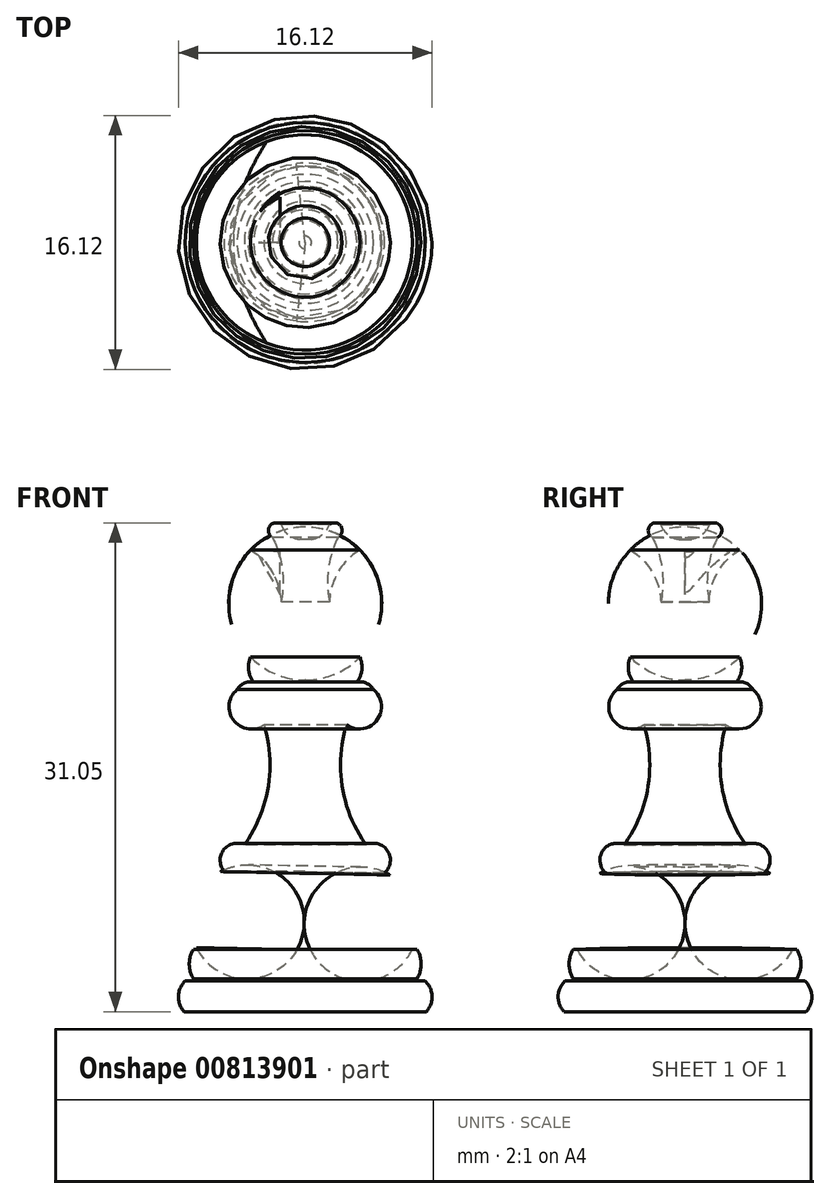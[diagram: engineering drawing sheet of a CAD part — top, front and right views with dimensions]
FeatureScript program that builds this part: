
annotation { "Feature Type Name" : "Feature", "Feature Type Description" : "" }
export const myFeature = defineFeature(function(context is Context, id is Id, definition is map)
    precondition{}
    {
        {
            var Q0;
            Q0=qCreatedBy(makeId("Front.planeOp"),FACE);
            var sketch = newSketch(context, id + "F0", { "sketchPlane" : qUnion([Q0])});
            skArc(sketch, "E0", {"start": v(-7.62, 1.95) * mm, "mid": v(-8.05, 0.99) * mm, "end": v(-7.7, 0) * mm});
            skLineSegment(sketch, "E1", {"start": v(-7.62, 1.95) * mm, "end": v(0, 1.95) * mm});
            skLineSegment(sketch, "E2", {"start": v(0, 1.95) * mm, "end": v(0, 0) * mm});
            skLineSegment(sketch, "E3", {"start": v(0, 0) * mm, "end": v(-7.7, 0) * mm});
            skSolve(sketch);
        }
        {
            var Q0;
            Q0 = qSketchRegion(id + "F0", true);
            var Q1;
            Q1=sQuery(id+"F0.wireOp",EDGE,"E2");
            revolve(context, id + "F1", {"surfaceOperationType" : NewSurfaceOperationType.NEW, "entities" : qUnion([Q0]), "axis" : qUnion([Q1]), "revolveType" : RevolveType.FULL});
        }
        {
            var Q0;
            Q0=qCreatedBy(makeId("Front.planeOp"),FACE);
            var sketch = newSketch(context, id + "F2", { "sketchPlane" : qUnion([Q0])});
            skLineSegment(sketch, "E4", {"start": v(0, 2.09) * mm, "end": v(-7.1, 2.09) * mm});
            skArc(sketch, "E5", {"start": v(-7.1, 3.97) * mm, "mid": v(-7.36, 3.03) * mm, "end": v(-7.1, 2.09) * mm});
            skLineSegment(sketch, "E6", {"start": v(-7.1, 3.97) * mm, "end": v(0, 3.97) * mm});
            skLineSegment(sketch, "E7", {"start": v(0, 3.97) * mm, "end": v(0, 2.09) * mm});
            skSolve(sketch);
        }
        {
            var Q0;
            Q0 = qSketchRegion(id + "F2", true);
            var Q1;
            Q1=sQuery(id+"F2.wireOp",EDGE,"E7");
            revolve(context, id + "F3", {"surfaceOperationType" : NewSurfaceOperationType.NEW, "entities" : qUnion([Q0]), "axis" : qUnion([Q1]), "revolveType" : RevolveType.FULL});
        }
        {
            var Q0;
            Q0=qCreatedBy(makeId("Front.planeOp"),FACE);
            var sketch = newSketch(context, id + "F4", { "sketchPlane" : qUnion([Q0])});
            skArc(sketch, "E8", {"start": v(-5.4, 8.9) * mm, "mid": v(-7.14, 6.79) * mm, "end": v(-6.91, 4.06) * mm});
            skLineSegment(sketch, "E9", {"start": v(-5.4, 8.9) * mm, "end": v(0, 8.9) * mm});
            skLineSegment(sketch, "E10", {"start": v(0, 8.9) * mm, "end": v(-0.1, 3.8) * mm});
            skLineSegment(sketch, "E11", {"start": v(-0.1, 3.8) * mm, "end": v(-6.91, 4.06) * mm});
            skSolve(sketch);
        }
        {
            var Q0;
            Q0 = qSketchRegion(id + "F4", true);
            var Q1;
            Q1=sQuery(id+"F4.wireOp",EDGE,"E10");
            revolve(context, id + "F5", {"operationType" : NewBodyOperationType.ADD, "surfaceOperationType" : NewSurfaceOperationType.NEW, "entities" : qUnion([Q0]), "axis" : qUnion([Q1]), "revolveType" : RevolveType.FULL});
        }
        {
            var Q0;
            Q0=qCreatedBy(makeId("Front.planeOp"),FACE);
            var sketch = newSketch(context, id + "F6", { "sketchPlane" : qUnion([Q0])});
            skArc(sketch, "E12", {"start": v(-3.87, 10.6) * mm, "mid": v(-5.23, 10.21) * mm, "end": v(-5.03, 8.8) * mm});
            skArc(sketch, "E13", {"start": v(-3.87, 10.6) * mm, "mid": v(-2.35, 14.26) * mm, "end": v(-2.61, 18.22) * mm});
            skArc(sketch, "E14", {"start": v(-4.33, 20.46) * mm, "mid": v(-4.55, 18.5) * mm, "end": v(-2.61, 18.22) * mm});
            skArc(sketch, "E15", {"start": v(-2.61, 20.46) * mm, "mid": v(-3.47, 20.96) * mm, "end": v(-4.33, 20.46) * mm});
            skArc(sketch, "E16", {"start": v(-3.47, 22.52) * mm, "mid": v(-3.49, 21.3) * mm, "end": v(-2.61, 20.46) * mm});
            skPoint(sketch, "E16.startSnap0", {"position": v(-3.47, 20.96) * mm});
            skArc(sketch, "E17", {"start": v(-3.47, 29.33) * mm, "mid": v(-4.86, 25.92) * mm, "end": v(-3.47, 22.52) * mm});
            skArc(sketch, "E18", {"start": v(-1.54, 26.01) * mm, "mid": v(-2.08, 27.92) * mm, "end": v(-3.47, 29.33) * mm});
            skArc(sketch, "E19", {"start": v(-1.54, 26.01) * mm, "mid": v(-1.46, 28.12) * mm, "end": v(-2.08, 30.13) * mm});
            skPoint(sketch, "E19.endSnap0", {"position": v(-2.08, 27.92) * mm});
            skArc(sketch, "E20", {"start": v(-1.54, 30.94) * mm, "mid": v(-2.26, 30.84) * mm, "end": v(-2.08, 30.13) * mm});
            skArc(sketch, "E21", {"start": v(0, 32.82) * mm, "mid": v(-1.3, 32.31) * mm, "end": v(-1.54, 30.94) * mm});
            skLineSegment(sketch, "E22", {"start": v(0, 32.82) * mm, "end": v(0, 8.9) * mm});
            skLineSegment(sketch, "E23", {"start": v(0, 8.9) * mm, "end": v(-5.03, 8.8) * mm});
            skSolve(sketch);
        }
        {
            var Q0;
            Q0 = qSketchRegion(id + "F6", true);
            var Q1;
            Q1=sQuery(id+"F6.wireOp",EDGE,"E22");
            revolve(context, id + "F7", {"operationType" : NewBodyOperationType.ADD, "surfaceOperationType" : NewSurfaceOperationType.NEW, "entities" : qUnion([Q0]), "axis" : qUnion([Q1]), "revolveType" : RevolveType.FULL});
        }
        {
            var Q0;
            Q0=qCreatedBy(makeId("Front.planeOp"),FACE);
            var sketch = newSketch(context, id + "F8", { "sketchPlane" : qUnion([Q0])});
            skLineSegment(sketch, "E24", {"start": v(-3.19, 29.36) * mm, "end": v(-1.6, 26.5) * mm});
            skLineSegment(sketch, "E25", {"start": v(-1.6, 26.5) * mm, "end": v(-1.6, 29.2) * mm});
            skLineSegment(sketch, "E26", {"start": v(-1.6, 29.2) * mm, "end": v(-3.19, 29.36) * mm});
            skSolve(sketch);
        }
        {
            var Q0;
            Q0 = qSketchRegion(id + "F8", true);
            extrude(context, id + "F9", {"entities" : qUnion([Q0]), "operationType" : NewBodyOperationType.REMOVE, "oppositeDirection" : true, "depth" : 23.44 * mm, "offsetDistance" : 25.4 * mm});
        }
    });
